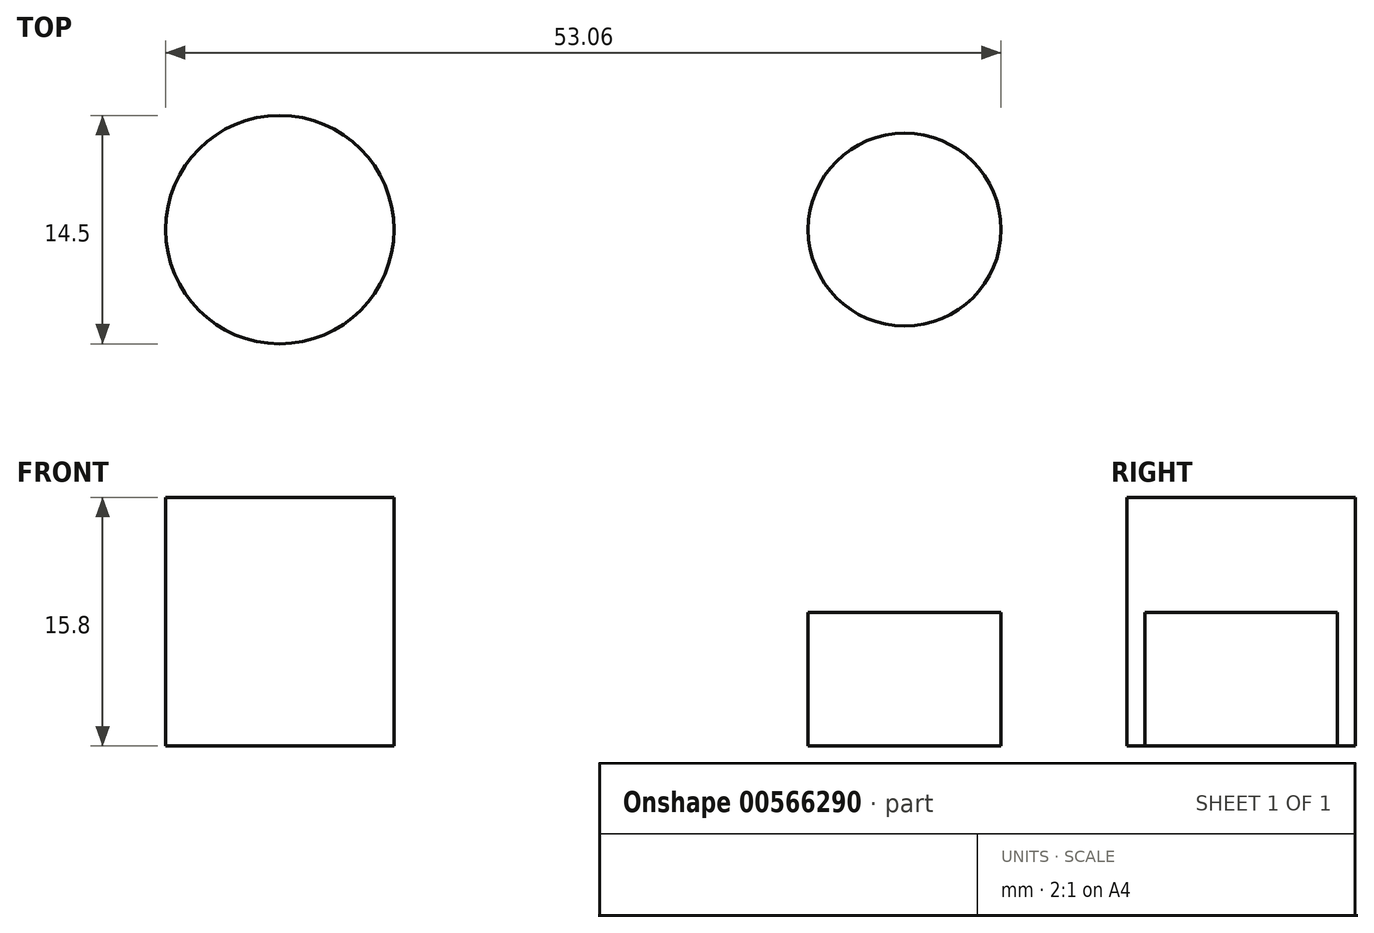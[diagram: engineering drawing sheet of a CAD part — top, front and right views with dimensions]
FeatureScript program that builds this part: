
annotation { "Feature Type Name" : "Feature", "Feature Type Description" : "" }
export const myFeature = defineFeature(function(context is Context, id is Id, definition is map)
    precondition{}
    {
        {
            var Q0;
            Q0=qCreatedBy(makeId("Top.planeOp"),FACE);
            var sketch = newSketch(context, id + "F0", { "sketchPlane" : qUnion([Q0])});
            skCircle(sketch, "E0", {"center": v(-21.44, 0) * mm, "radius": 7.25 * mm});
            skSolve(sketch);
        }
        {
            var Q0;
            Q0=makeQuery(id+"F0.imprint","IMPRINT",FACE,{"disambiguationData":[TD([[makeQuery(id+"F0.imprint","IMPRINT",EDGE,{"derivedFrom":sQuery(id+"F0.wireOp",EDGE,"E0")}),1.0]])]});
            var Q1;
            Q1=sQuery(id+"F0.wireOp",EDGE,"E0");
            extrude(context, id + "F1", {"entities" : qUnion([Q0]), "surfaceEntities" : qUnion([Q1]), "depth" : 15.8 * mm, "offsetDistance" : 25 * mm});
        }
        {
            var Q0;
            Q0=qCreatedBy(makeId("Top.planeOp"),FACE);
            var sketch = newSketch(context, id + "F2", { "sketchPlane" : qUnion([Q0])});
            skCircle(sketch, "E1", {"center": v(18.25, 0) * mm, "radius": 6.13 * mm});
            skSolve(sketch);
        }
        {
            var Q0;
            Q0 = qSketchRegion(id + "F2", true);
            extrude(context, id + "F3", {"entities" : qUnion([Q0]), "depth" : 8.5 * mm, "offsetDistance" : 25 * mm});
        }
    });
